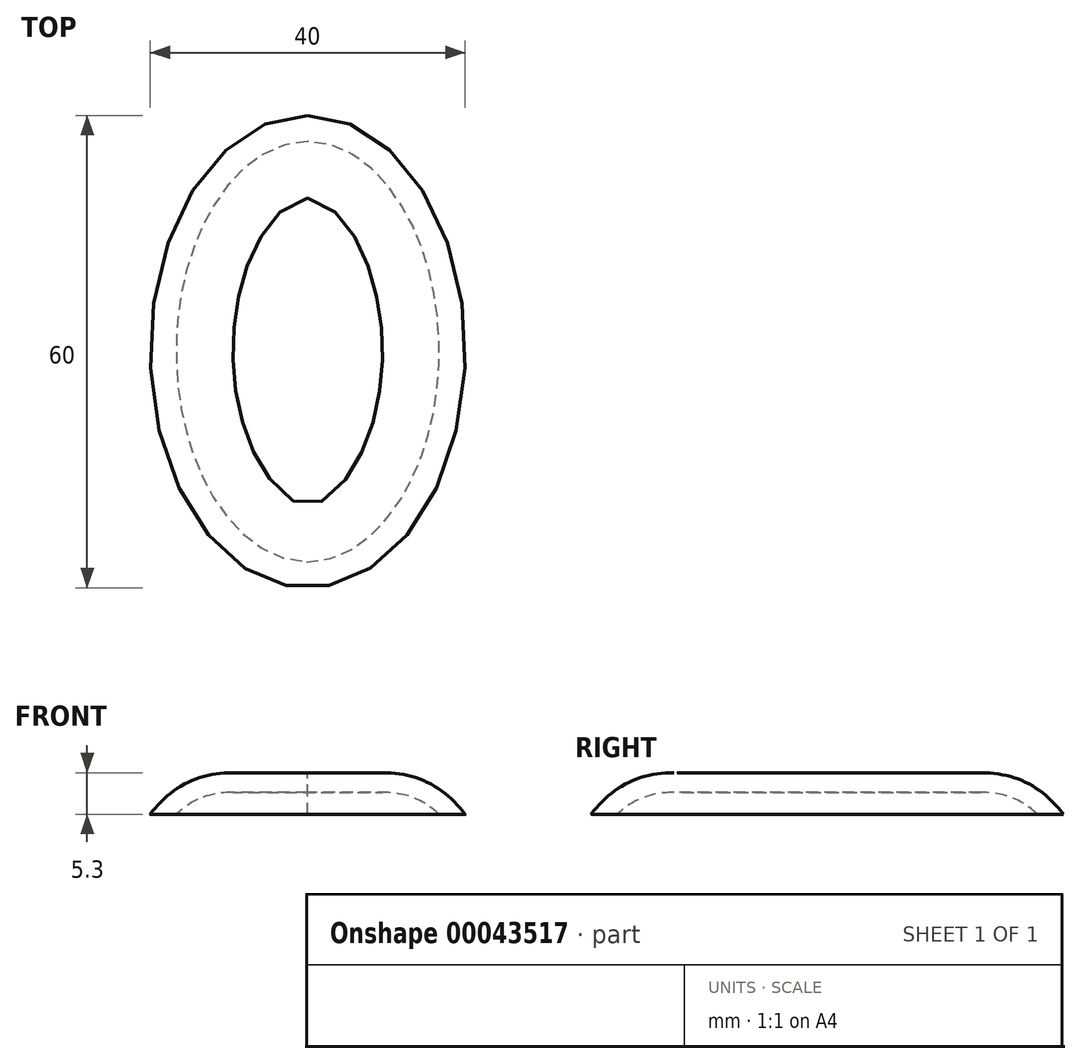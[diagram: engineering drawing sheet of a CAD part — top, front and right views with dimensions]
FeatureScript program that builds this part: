
annotation { "Feature Type Name" : "Feature", "Feature Type Description" : "" }
export const myFeature = defineFeature(function(context is Context, id is Id, definition is map)
    precondition{}
    {
        {
            var Q0;
            Q0=qCreatedBy(makeId("Top.planeOp"),FACE);
            var sketch = newSketch(context, id + "F0", { "sketchPlane" : qUnion([Q0])});
            skEllipse(sketch, "E0", {"center": v(-0.56, 0.19) * mm, "majorRadius": 30 * mm, "minorRadius": 20 * mm, "majorAxis": v(0, 1)});
            skSolve(sketch);
        }
        {
            var Q0;
            Q0=makeQuery(id+"F0.imprint","IMPRINT",FACE,{"disambiguationData":[TD([[makeQuery(id+"F0.imprint","IMPRINT",EDGE,{"derivedFrom":sQuery(id+"F0.wireOp",EDGE,"E0")}),1.0]])]});
            extrude(context, id + "F1", {"entities" : qUnion([Q0]), "depth" : 5.3 * mm, "offsetDistance" : 25 * mm});
        }
        {
            var Q0;
            Q0=makeQuery(id+"F1.opExtrude","CAP_EDGE",EDGE,{"disambiguationData":[OSD([sQuery(id+"F0.wireOp",EDGE,"E0")])],"isStart":false});
            fillet(context, id + "F2", {"entities" : qUnion([Q0]), "radius" : 13.04 * mm, "tangentPropagation" : true, "rho" : 0.5, "crossSection" : FilletCrossSection.CONIC, "allowEdgeOverflow" : false});
        }
        {
            var Q0;
            Q0=makeQuery(id+"F1.opExtrude","CAP_FACE",FACE,{"disambiguationData":[OSD([sQuery(id+"F0.wireOp",EDGE,"E0")])],"isStart":true});
            shell(context, id + "F3", {"entities" : qUnion([Q0]), "thickness" : 2.5 * mm});
        }
        {
            var Q0;
            Q0=qCreatedBy(makeId("Top.planeOp"),FACE);
            cPlane(context, id + "F4", {"entities" : qUnion([Q0]), "cplaneType" : CPlaneType.OFFSET, "offset" : 5.3 * mm, "width" : 150 * mm, "height" : 150 * mm});
        }
    });
